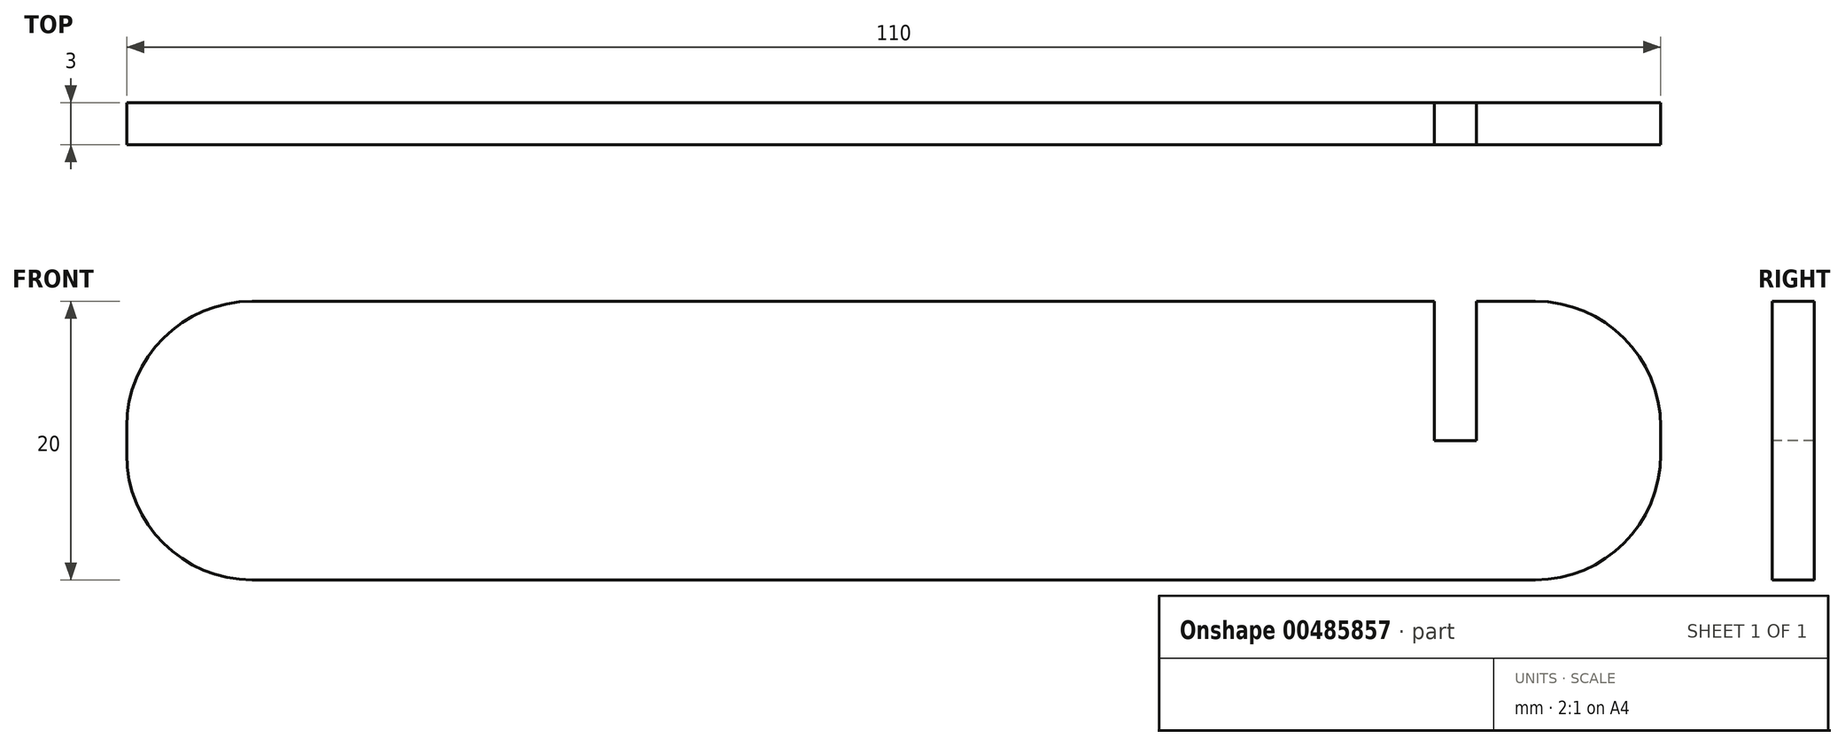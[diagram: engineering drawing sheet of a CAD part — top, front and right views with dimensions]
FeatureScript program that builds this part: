
annotation { "Feature Type Name" : "Feature", "Feature Type Description" : "" }
export const myFeature = defineFeature(function(context is Context, id is Id, definition is map)
    precondition{}
    {
        {
            var Q0;
            Q0=qCreatedBy(makeId("Front.planeOp"),FACE);
            var sketch = newSketch(context, id + "F0", { "sketchPlane" : qUnion([Q0])});
            skLineSegment(sketch, "E0.bottom", {"start": v(4.6, 0) * mm, "end": v(114.6, 0) * mm});
            skLineSegment(sketch, "E0.top", {"start": v(4.6, 20) * mm, "end": v(114.6, 20) * mm});
            skLineSegment(sketch, "E0.left", {"start": v(4.6, 0) * mm, "end": v(4.6, 20) * mm});
            skLineSegment(sketch, "E0.right", {"start": v(114.6, 0) * mm, "end": v(114.6, 20) * mm});
            skSolve(sketch);
        }
        {
            var Q0;
            Q0=makeQuery(id+"F0.imprint","IMPRINT",FACE,{"disambiguationData":[TD([[makeQuery(id+"F0.imprint","IMPRINT",EDGE,{"derivedFrom":sQuery(id+"F0.wireOp",EDGE,"E0.bottom")}),1.0]])]});
            extrude(context, id + "F1", {"entities" : qUnion([Q0]), "depth" : 3 * mm});
        }
        {
            var Q0;
            Q0=makeQuery(id+"F1.opExtrude","SWEPT_EDGE",EDGE,{"disambiguationData":[OSD([sQuery(id+"F0.wireOp",EDGE,"E0.top"),sQuery(id+"F0.wireOp",EDGE,"E0.left")])]});
            var Q1;
            Q1=makeQuery(id+"F1.opExtrude","SWEPT_EDGE",EDGE,{"disambiguationData":[OSD([sQuery(id+"F0.wireOp",EDGE,"E0.bottom"),sQuery(id+"F0.wireOp",EDGE,"E0.left")])]});
            var Q2;
            Q2=makeQuery(id+"F1.opExtrude","SWEPT_EDGE",EDGE,{"disambiguationData":[OSD([sQuery(id+"F0.wireOp",EDGE,"E0.top"),sQuery(id+"F0.wireOp",EDGE,"E0.right")])]});
            var Q3;
            Q3=makeQuery(id+"F1.opExtrude","SWEPT_EDGE",EDGE,{"disambiguationData":[OSD([sQuery(id+"F0.wireOp",EDGE,"E0.bottom"),sQuery(id+"F0.wireOp",EDGE,"E0.right")])]});
            fillet(context, id + "F2", {"entities" : qUnion([Q0, Q1, Q2, Q3]), "radius" : 9 * mm, "tangentPropagation" : true, "allowEdgeOverflow" : false});
        }
        {
            var Q0;
            Q0=makeQuery(id+"F1.opExtrude","CAP_FACE",FACE,{"disambiguationData":[OSD([sQuery(id+"F0.wireOp",EDGE,"E0.bottom"),sQuery(id+"F0.wireOp",EDGE,"E0.top"),sQuery(id+"F0.wireOp",EDGE,"E0.left"),sQuery(id+"F0.wireOp",EDGE,"E0.right")])],"isStart":false});
            var sketch = newSketch(context, id + "F3", { "sketchPlane" : qUnion([Q0])});
            skLineSegment(sketch, "E1.bottom", {"start": v(98.38, 20) * mm, "end": v(101.38, 20) * mm});
            skLineSegment(sketch, "E1.top", {"start": v(98.38, 10) * mm, "end": v(101.38, 10) * mm});
            skLineSegment(sketch, "E1.left", {"start": v(98.38, 20) * mm, "end": v(98.38, 10) * mm});
            skLineSegment(sketch, "E1.right", {"start": v(101.38, 20) * mm, "end": v(101.38, 10) * mm});
            skSolve(sketch);
        }
        {
            var Q0;
            Q0=makeQuery(id+"F3.imprint","IMPRINT",FACE,{"disambiguationData":[TD([[makeQuery(id+"F3.imprint","IMPRINT",EDGE,{"derivedFrom":sQuery(id+"F3.wireOp",EDGE,"E1.bottom")}),-1.0]])]});
            extrude(context, id + "F4", {"entities" : qUnion([Q0]), "operationType" : NewBodyOperationType.REMOVE, "oppositeDirection" : true, "depth" : 3 * mm});
        }
    });
